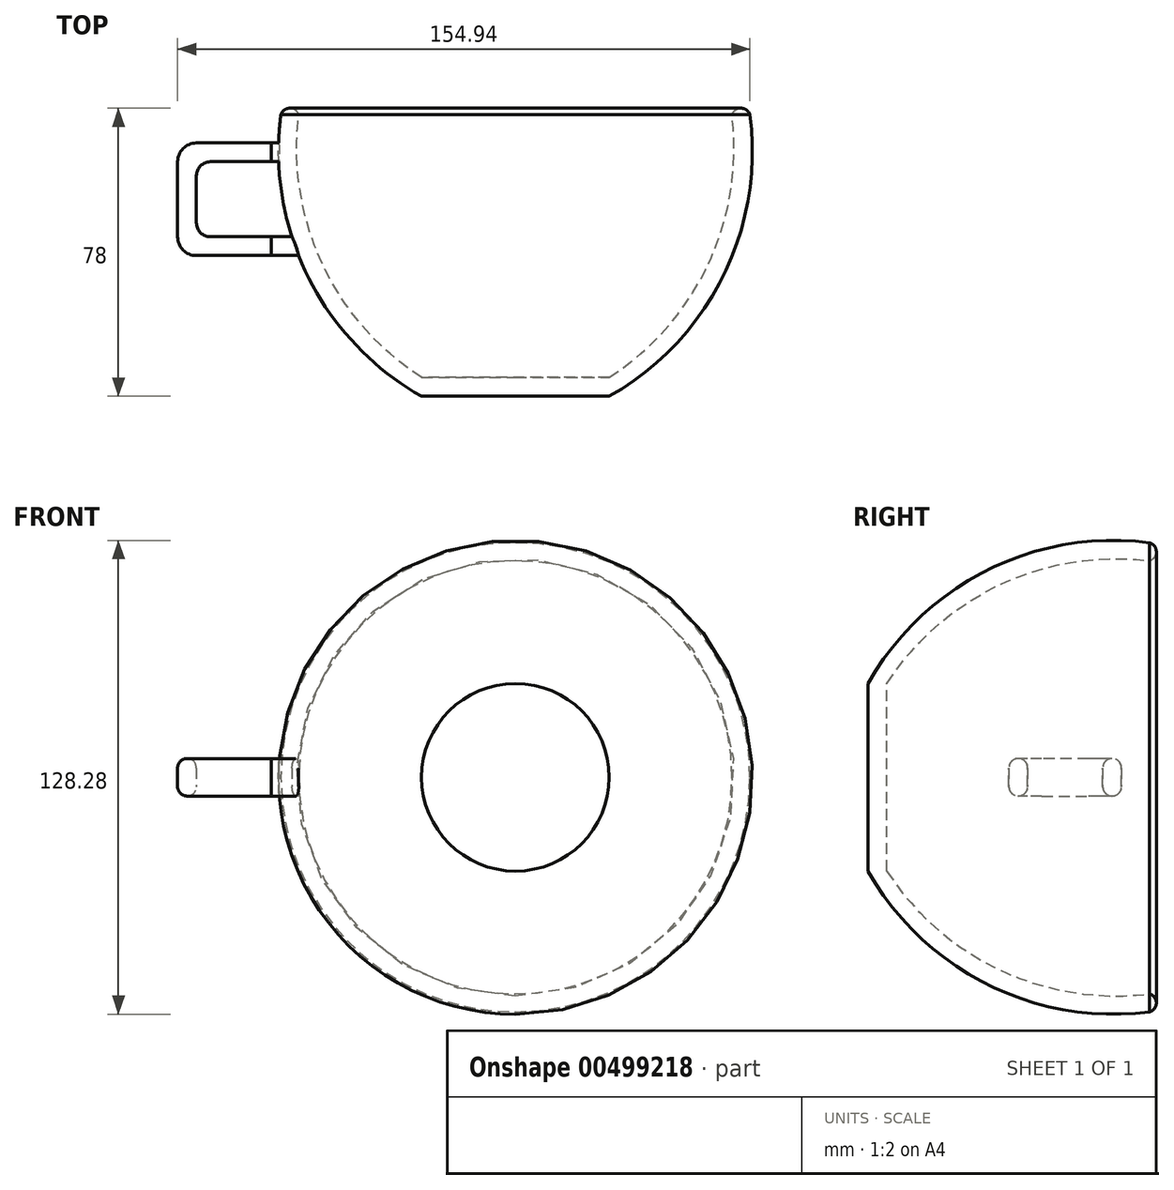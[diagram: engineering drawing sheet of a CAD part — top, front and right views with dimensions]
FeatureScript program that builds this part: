
annotation { "Feature Type Name" : "Feature", "Feature Type Description" : "" }
export const myFeature = defineFeature(function(context is Context, id is Id, definition is map)
    precondition{}
    {
        {
            var Q0;
            Q0=qCreatedBy(makeId("Top.planeOp"),FACE);
            var sketch = newSketch(context, id + "F0", { "sketchPlane" : qUnion([Q0])});
            skLineSegment(sketch, "E0", {"start": v(0, -38.1) * mm, "end": v(-25.4, -38.1) * mm});
            skArc(sketch, "E1", {"start": v(-63.5, 38.1) * mm, "mid": v(-56.1, -5.82) * mm, "end": v(-25.4, -38.1) * mm});
            skArc(sketch, "E2", {"start": v(-58.64, 38.1) * mm, "mid": v(-61.07, 39.9) * mm, "end": v(-63.5, 38.1) * mm});
            skPoint(sketch, "E3.end.orphan", {"position": v(-25.4, -35.56) * mm});
            skLineSegment(sketch, "E4", {"start": v(0, -38.1) * mm, "end": v(0, -33.02) * mm});
            skLineSegment(sketch, "E5", {"start": v(0, -33.02) * mm, "end": v(-25.4, -33.02) * mm});
            skArc(sketch, "E6", {"start": v(-58.64, 38.1) * mm, "mid": v(-52.26, -2.25) * mm, "end": v(-25.4, -33.02) * mm});
            skSolve(sketch);
        }
        {
            var Q0;
            Q0=qCreatedBy(makeId("Top.planeOp"),FACE);
            var sketch = newSketch(context, id + "F1", { "sketchPlane" : qUnion([Q0])});
            skLineSegment(sketch, "E7", {"start": v(0, 0) * mm, "end": v(0, -38.1) * mm});
            skLineSegment(sketch, "E8", {"start": v(0, -38.1) * mm, "end": v(0, 38.1) * mm});
            skSolve(sketch);
        }
        {
            var Q0;
            Q0=makeQuery(id+"F0.imprint","IMPRINT",FACE,{"disambiguationData":[TD([[makeQuery(id+"F0.imprint","IMPRINT",EDGE,{"derivedFrom":sQuery(id+"F0.wireOp",EDGE,"E0")}),-1.0]])]});
            var Q1;
            Q1 = qSketchRegion(id + "F1", true);
            var Q2;
            Q2=sQuery(id+"F1.wireOp",EDGE,"E8");
            revolve(context, id + "F2", {"entities" : qUnion([Q0, Q1]), "axis" : qUnion([Q2]), "revolveType" : RevolveType.FULL});
        }
        {
            var Q0;
            Q0=qCreatedBy(makeId("Top.planeOp"),FACE);
            var sketch = newSketch(context, id + "F3", { "sketchPlane" : qUnion([Q0])});
            skLineSegment(sketch, "E9", {"start": v(-66.04, 30.48) * mm, "end": v(-91.44, 30.48) * mm});
            skLineSegment(sketch, "E10", {"start": v(-91.44, 30.48) * mm, "end": v(-91.44, 0) * mm});
            skLineSegment(sketch, "E11", {"start": v(-91.44, 0) * mm, "end": v(-66.04, 0) * mm});
            skLineSegment(sketch, "E12", {"start": v(-66.04, 0) * mm, "end": v(-66.04, 5.08) * mm});
            skLineSegment(sketch, "E13", {"start": v(-66.04, 5.08) * mm, "end": v(-82.55, 5.08) * mm});
            skLineSegment(sketch, "E14", {"start": v(-86.36, 8.9) * mm, "end": v(-86.36, 21.59) * mm});
            skLineSegment(sketch, "E15", {"start": v(-82.55, 25.4) * mm, "end": v(-66.04, 25.4) * mm});
            skLineSegment(sketch, "E16", {"start": v(-66.04, 25.4) * mm, "end": v(-66.04, 30.48) * mm});
            skPoint(sketch, "E17.visualSharp", {"position": v(-86.36, 25.4) * mm});
            skArc(sketch, "E17.filletArc", {"start": v(-82.55, 25.4) * mm, "mid": v(-85.24, 24.28) * mm, "end": v(-86.36, 21.59) * mm});
            skPoint(sketch, "E18.visualSharp", {"position": v(-86.36, 5.08) * mm});
            skArc(sketch, "E18.filletArc", {"start": v(-86.36, 8.9) * mm, "mid": v(-85.24, 6.2) * mm, "end": v(-82.55, 5.08) * mm});
            skSolve(sketch);
        }
        {
            var Q0;
            Q0 = qSketchRegion(id + "F3", true);
            extrude(context, id + "F4", {"entities" : qUnion([Q0]), "depth" : 5.08 * mm});
        }
        {
            var Q0;
            Q0 = qSketchRegion(id + "F3", true);
            extrude(context, id + "F5", {"entities" : qUnion([Q0]), "operationType" : NewBodyOperationType.ADD, "oppositeDirection" : true, "depth" : 5.08 * mm});
        }
        {
            var Q0;
            {var subQ0=sQuery(id+"F3.wireOp",EDGE,"E10");var subQ1=sQuery(id+"F3.wireOp",EDGE,"E9");Q0=makeQuery(id+"F5.boolean.opBoolean","MERGE",EDGE,{"derivedFrom":[makeQuery(id+"F4.opExtrude","SWEPT_EDGE",EDGE,{"disambiguationData":[OSD([subQ1,subQ0])]}),makeQuery(id+"F5.opExtrude","SWEPT_EDGE",EDGE,{"disambiguationData":[OSD([subQ1,subQ0])]})]});}
            fillet(context, id + "F6", {"entities" : qUnion([Q0]), "radius" : 5.08 * mm, "tangentPropagation" : true, "allowEdgeOverflow" : false});
        }
        {
            var Q0;
            {var subQ0=sQuery(id+"F3.wireOp",EDGE,"E11");var subQ1=sQuery(id+"F3.wireOp",EDGE,"E10");Q0=makeQuery(id+"F5.boolean.opBoolean","MERGE",EDGE,{"derivedFrom":[makeQuery(id+"F4.opExtrude","SWEPT_EDGE",EDGE,{"disambiguationData":[OSD([subQ1,subQ0])]}),makeQuery(id+"F5.opExtrude","SWEPT_EDGE",EDGE,{"disambiguationData":[OSD([subQ1,subQ0])]})]});}
            fillet(context, id + "F7", {"entities" : qUnion([Q0]), "radius" : 5.08 * mm, "tangentPropagation" : true, "allowEdgeOverflow" : false});
        }
        {
            var Q0;
            Q0=makeQuery(id+"F4.opExtrude","CAP_EDGE",EDGE,{"disambiguationData":[OSD([sQuery(id+"F3.wireOp",EDGE,"E13")])],"isStart":false});
            fillet(context, id + "F8", {"entities" : qUnion([Q0]), "radius" : 2.54 * mm, "tangentPropagation" : true, "allowEdgeOverflow" : false});
        }
        {
            var Q0;
            Q0=makeQuery(id+"F5.opExtrude","CAP_EDGE",EDGE,{"disambiguationData":[OSD([sQuery(id+"F3.wireOp",EDGE,"E13")])],"isStart":false});
            fillet(context, id + "F9", {"entities" : qUnion([Q0]), "radius" : 2.54 * mm, "tangentPropagation" : true, "allowEdgeOverflow" : false});
        }
        {
            var Q0;
            Q0=makeQuery(id+"F5.opExtrude","CAP_EDGE",EDGE,{"disambiguationData":[OSD([sQuery(id+"F3.wireOp",EDGE,"E9")])],"isStart":false});
            fillet(context, id + "F10", {"entities" : qUnion([Q0]), "radius" : 2.54 * mm, "tangentPropagation" : true, "allowEdgeOverflow" : false});
        }
        {
            var Q0;
            Q0=makeQuery(id+"F4.opExtrude","CAP_EDGE",EDGE,{"disambiguationData":[OSD([sQuery(id+"F3.wireOp",EDGE,"E9")])],"isStart":false});
            fillet(context, id + "F11", {"entities" : qUnion([Q0]), "radius" : 2.54 * mm, "tangentPropagation" : true, "allowEdgeOverflow" : false});
        }
        {
            var Q0;
            {var subQ0=sQuery(id+"F3.wireOp",EDGE,"E16");Q0=makeQuery(id+"F5.boolean.opBoolean","MERGE",FACE,{"derivedFrom":[makeQuery(id+"F4.opExtrude","SWEPT_FACE",FACE,{"disambiguationData":[OSD([subQ0])]}),makeQuery(id+"F5.opExtrude","SWEPT_FACE",FACE,{"disambiguationData":[OSD([subQ0])]})]});}
            var Q1;
            Q1=makeQuery(id+"F2.opRevolve","SWEPT_BODY",BODY,{"disambiguationData":[OSD([sQuery(id+"F0.wireOp",EDGE,"E0"),sQuery(id+"F0.wireOp",EDGE,"E1"),sQuery(id+"F0.wireOp",EDGE,"E2"),sQuery(id+"F0.wireOp",EDGE,"E4"),sQuery(id+"F0.wireOp",EDGE,"E5"),sQuery(id+"F0.wireOp",EDGE,"E6")])]});
            extrude(context, id + "F12", {"entities" : qUnion([Q0]), "endBound" : BoundingType.UP_TO_BODY, "endBoundEntityBody" : qUnion([Q1]), "depth" : 25.4 * mm});
        }
        {
            var Q0;
            {var subQ0=sQuery(id+"F3.wireOp",EDGE,"E12");Q0=makeQuery(id+"F5.boolean.opBoolean","MERGE",FACE,{"derivedFrom":[makeQuery(id+"F4.opExtrude","SWEPT_FACE",FACE,{"disambiguationData":[OSD([subQ0])]}),makeQuery(id+"F5.opExtrude","SWEPT_FACE",FACE,{"disambiguationData":[OSD([subQ0])]})]});}
            var Q1;
            Q1=makeQuery(id+"F2.opRevolve","SWEPT_BODY",BODY,{"disambiguationData":[OSD([sQuery(id+"F0.wireOp",EDGE,"E0"),sQuery(id+"F0.wireOp",EDGE,"E1"),sQuery(id+"F0.wireOp",EDGE,"E2"),sQuery(id+"F0.wireOp",EDGE,"E4"),sQuery(id+"F0.wireOp",EDGE,"E5"),sQuery(id+"F0.wireOp",EDGE,"E6")])]});
            extrude(context, id + "F13", {"entities" : qUnion([Q0]), "endBound" : BoundingType.UP_TO_BODY, "endBoundEntityBody" : qUnion([Q1]), "depth" : 25.4 * mm});
        }
    });
